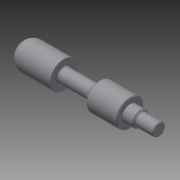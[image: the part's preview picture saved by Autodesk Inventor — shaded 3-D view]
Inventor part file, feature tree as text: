
AUTODESK INVENTOR PART (.ipt)
format: ipt  version: 2014 SP1 (Build 180222100, 222)  size: 125,440 bytes
history: native  units: in
note: dims shown in document units (in); Inventor stores cm internally (conversion verified against a paired STEP export)
features: revolve x1, chamfer x1, fillet x1, sketch x1
ambient origin geometry x8: Origin, YZ Plane, XZ Plane, XY Plane, X Axis, Y Axis, Z Axis, Center Point
bodies: Solid1 (feature_tree)
feature tree (4):
  revolve  "Revolution1"  [1 undecoded]
  chamfer  "Chamfer1"  Distance=0.0855in
  fillet  "Fillet1"  [1 undecoded]
  sketch  "Sketch1"  dims[d0=0.1875in d1=0.95in d2=0.0781in d3=0.0855in d4=45.0deg d5=0.0935in d6=45.0deg d7=0.2945in d8=0.109in d9=0.1875in d10=0.207in d11=0.119in d12=0.199in d13=90.0deg d14=0.005in d15=0.125in d16=45.0deg d17=0.01in]
note: 2 required parameter values undecoded (feature->parameter linkage not recoverable at this tier; creation-order binding heuristic only, values carry confidence <= 0.55)